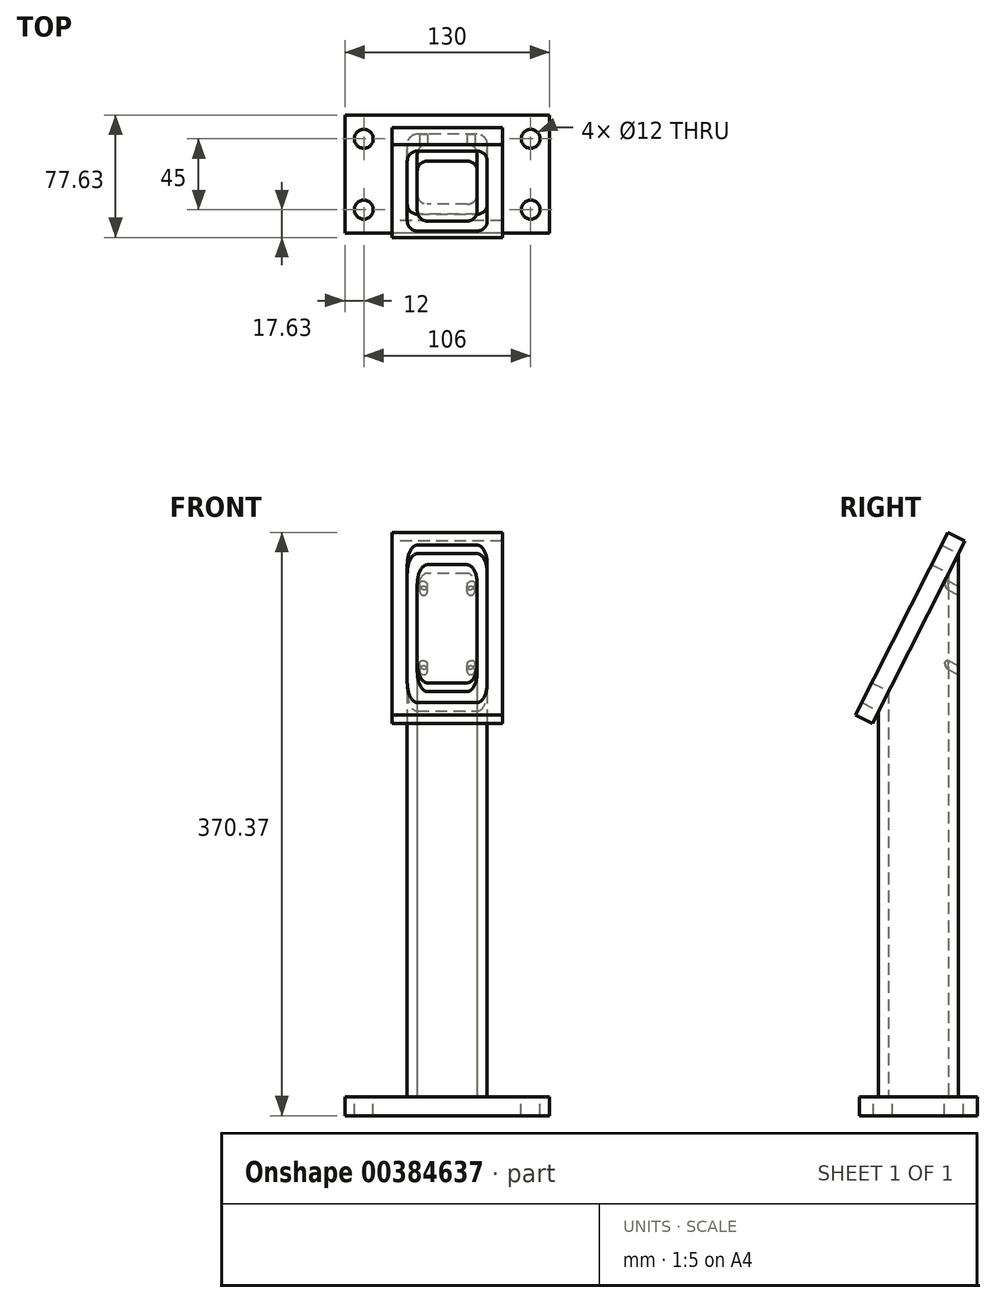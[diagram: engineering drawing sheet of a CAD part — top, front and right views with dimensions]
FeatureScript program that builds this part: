
annotation { "Feature Type Name" : "Feature", "Feature Type Description" : "" }
export const myFeature = defineFeature(function(context is Context, id is Id, definition is map)
    precondition{}
    {
        {
            var Q0;
            Q0=qCreatedBy(makeId("Top.planeOp"),FACE);
            var sketch = newSketch(context, id + "F0", { "sketchPlane" : qUnion([Q0])});
            skLineSegment(sketch, "E0.bottom", {"start": v(65, 37.5) * mm, "end": v(-65, 37.5) * mm});
            skLineSegment(sketch, "E0.top", {"start": v(65, -37.5) * mm, "end": v(-65, -37.5) * mm});
            skLineSegment(sketch, "E0.left", {"start": v(65, 37.5) * mm, "end": v(65, -37.5) * mm});
            skLineSegment(sketch, "E0.right", {"start": v(-65, 37.5) * mm, "end": v(-65, -37.5) * mm});
            skPoint(sketch, "E0.middle", {"position": v(0, 0) * mm});
            skSolve(sketch);
        }
        {
            var Q0;
            Q0=makeQuery(id+"F0.imprint","IMPRINT",FACE,{"disambiguationData":[TD([[makeQuery(id+"F0.imprint","IMPRINT",EDGE,{"derivedFrom":sQuery(id+"F0.wireOp",EDGE,"E0.bottom")}),1.0]])]});
            extrude(context, id + "F1", {"entities" : qUnion([Q0]), "depth" : -12 * mm});
        }
        {
            var Q0;
            Q0=makeQuery(id+"F1.opExtrude","CAP_FACE",FACE,{"disambiguationData":[OSD([sQuery(id+"F0.wireOp",EDGE,"E0.bottom"),sQuery(id+"F0.wireOp",EDGE,"E0.top"),sQuery(id+"F0.wireOp",EDGE,"E0.left"),sQuery(id+"F0.wireOp",EDGE,"E0.right")])],"isStart":true});
            var sketch = newSketch(context, id + "F2", { "sketchPlane" : qUnion([Q0])});
            skLineSegment(sketch, "E1.bottom", {"start": v(19.05, -25.4) * mm, "end": v(-19.05, -25.4) * mm});
            skLineSegment(sketch, "E1.top", {"start": v(19.05, 25.4) * mm, "end": v(-19.05, 25.4) * mm});
            skLineSegment(sketch, "E1.left", {"start": v(25.4, -19.05) * mm, "end": v(25.4, 19.05) * mm});
            skLineSegment(sketch, "E1.right", {"start": v(-25.4, -19.05) * mm, "end": v(-25.4, 19.05) * mm});
            skPoint(sketch, "E1.middle", {"position": v(0, 0) * mm});
            skPoint(sketch, "E2.visualSharp", {"position": v(-25.4, -25.4) * mm});
            skArc(sketch, "E2.filletArc", {"start": v(-25.4, -19.05) * mm, "mid": v(-23.54, -23.54) * mm, "end": v(-19.05, -25.4) * mm});
            skPoint(sketch, "E3.visualSharp", {"position": v(-25.4, 25.4) * mm});
            skArc(sketch, "E3.filletArc", {"start": v(-19.05, 25.4) * mm, "mid": v(-23.54, 23.54) * mm, "end": v(-25.4, 19.05) * mm});
            skPoint(sketch, "E4.visualSharp", {"position": v(25.4, 25.4) * mm});
            skArc(sketch, "E4.filletArc", {"start": v(25.4, 19.05) * mm, "mid": v(23.54, 23.54) * mm, "end": v(19.05, 25.4) * mm});
            skPoint(sketch, "E5.visualSharp", {"position": v(25.4, -25.4) * mm});
            skArc(sketch, "E5.filletArc", {"start": v(19.05, -25.4) * mm, "mid": v(23.54, -23.54) * mm, "end": v(25.4, -19.05) * mm});
            skLineSegment(sketch, "E6.bottom", {"start": v(12.7, 19.05) * mm, "end": v(-12.7, 19.05) * mm});
            skLineSegment(sketch, "E6.top", {"start": v(12.7, -19.05) * mm, "end": v(-12.7, -19.05) * mm});
            skLineSegment(sketch, "E6.left", {"start": v(19.05, 12.7) * mm, "end": v(19.05, -12.7) * mm});
            skLineSegment(sketch, "E6.right", {"start": v(-19.05, 12.7) * mm, "end": v(-19.05, -12.7) * mm});
            skArc(sketch, "E7.filletArc", {"start": v(-12.7, 19.05) * mm, "mid": v(-17.2, 17.2) * mm, "end": v(-19.05, 12.7) * mm});
            skArc(sketch, "E8.filletArc", {"start": v(19.05, 12.7) * mm, "mid": v(17.2, 17.2) * mm, "end": v(12.7, 19.05) * mm});
            skArc(sketch, "E9.filletArc", {"start": v(12.7, -19.05) * mm, "mid": v(17.2, -17.2) * mm, "end": v(19.05, -12.7) * mm});
            skArc(sketch, "E10.filletArc", {"start": v(-19.05, -12.7) * mm, "mid": v(-17.2, -17.2) * mm, "end": v(-12.7, -19.05) * mm});
            skSolve(sketch);
        }
        {
            var Q0;
            Q0=qSketchRegion(id+"F2",true);
            extrude(context, id + "F3", {"entities" : qUnion([Q0]), "operationType" : NewBodyOperationType.ADD, "depth" : 345 * mm});
        }
        {
            var Q0;
            {var subQ0=sQuery(id+"F0.wireOp",EDGE,"E0.left");var subQ1=sQuery(id+"F0.wireOp",EDGE,"E0.bottom");var subQ2=sQuery(id+"F0.wireOp",EDGE,"E0.right");var subQ3=sQuery(id+"F0.wireOp",EDGE,"E0.top");Q0=makeQuery(id+"F3.boolean.opBoolean","SPLIT",FACE,{"disambiguationData":[TD([makeQuery(id+"F1.opExtrude","SWEPT_FACE",FACE,{"disambiguationData":[OSD([subQ1])]})])],"derivedFrom":makeQuery(id+"F1.opExtrude","CAP_FACE",FACE,{"disambiguationData":[OSD([subQ1,subQ3,subQ0,subQ2])],"isStart":true})});}
            var sketch = newSketch(context, id + "F4", { "sketchPlane" : qUnion([Q0])});
            skLineSegment(sketch, "E11", {"start": v(-65, -37.5) * mm, "end": v(-53, -37.5) * mm, "construction": true});
            skLineSegment(sketch, "E12", {"start": v(-53, -37.5) * mm, "end": v(-53, -22.5) * mm, "construction": true});
            skLineSegment(sketch, "E13", {"start": v(-65, 37.5) * mm, "end": v(-53, 37.5) * mm, "construction": true});
            skLineSegment(sketch, "E14", {"start": v(-53, 37.5) * mm, "end": v(-53, 22.5) * mm, "construction": true});
            skLineSegment(sketch, "E15", {"start": v(65, 37.5) * mm, "end": v(53, 37.5) * mm, "construction": true});
            skLineSegment(sketch, "E16", {"start": v(65, -37.5) * mm, "end": v(53, -37.5) * mm, "construction": true});
            skLineSegment(sketch, "E17", {"start": v(53, -37.5) * mm, "end": v(53, -22.5) * mm, "construction": true});
            skLineSegment(sketch, "E18", {"start": v(53, 37.5) * mm, "end": v(53, 22.5) * mm, "construction": true});
            skSolve(sketch);
        }
        {
            var Q0;
            Q0=sQuery(id+"F4.wireOp",VERTEX,"E14.end");
            var Q1;
            Q1=sQuery(id+"F4.wireOp",VERTEX,"E18.end");
            var Q2;
            Q2=sQuery(id+"F4.wireOp",VERTEX,"E17.end");
            var Q3;
            Q3=sQuery(id+"F4.wireOp",VERTEX,"E12.end");
            var Q4;
            Q4=makeQuery(id+"F1.opExtrude","SWEPT_BODY",BODY,{"disambiguationData":[OSD([sQuery(id+"F0.wireOp",EDGE,"E0.bottom"),sQuery(id+"F0.wireOp",EDGE,"E0.top"),sQuery(id+"F0.wireOp",EDGE,"E0.left"),sQuery(id+"F0.wireOp",EDGE,"E0.right")])]});
            hole(context, id + "F5", {"style" : HoleStyle.SIMPLE, "endStyle" : HoleEndStyle.THROUGH, "holeDiameter" : 12 * mm, "isTappedThrough" : true, "tappedDepth" : 12 * mm, "tapClearance" : 3, "locations" : qUnion([Q0, Q1, Q2, Q3]), "scope" : qUnion([Q4])});
        }
        {
            var Q0;
            Q0=makeQuery(id+"F3.opExtrude","SWEPT_FACE",FACE,{"disambiguationData":[OSD([sQuery(id+"F2.wireOp",EDGE,"E1.left")])]});
            var sketch = newSketch(context, id + "F6", { "sketchPlane" : qUnion([Q0])});
            skLineSegment(sketch, "E19", {"start": v(-19.05, 345) * mm, "end": v(-25.4, 345) * mm, "construction": true});
            skLineSegment(sketch, "E20", {"start": v(-25.4, 345) * mm, "end": v(25.4, 345) * mm});
            skLineSegment(sketch, "E21", {"start": v(25.4, 345) * mm, "end": v(-25.4, 244.95) * mm});
            skLineSegment(sketch, "E22", {"start": v(-25.4, 345) * mm, "end": v(-25.4, 244.95) * mm});
            skSolve(sketch);
        }
        {
            var Q0;
            {var subQ3=sQuery(id+"F6.wireOp",EDGE,"E22");Q0=makeQuery(id+"F6.imprint","IMPRINT",FACE,{"disambiguationData":[TD([[makeQuery(id+"F6.imprint","IMPRINT",EDGE,{"derivedFrom":subQ3}),1.0]])]});}
            var Q1;
            {var subQ0=sQuery(id+"F6.wireOp",EDGE,"E20");var subQ1=sQuery(id+"F2.wireOp",EDGE,"E1.left");var subQ2=makeQuery(id+"F3.opExtrude","SWEPT_EDGE",EDGE,{"disambiguationData":[OSD([subQ1,sQuery(id+"F2.wireOp",EDGE,"E5.filletArc")])]});var subQ3=makeQuery(id+"F6.imprint","INTERSECT",VERTEX,{"derivedFrom":[subQ2,subQ0]});Q1=makeQuery(id+"F6.imprint","IMPRINT",FACE,{"disambiguationData":[TD([[makeQuery(id+"F6.imprint","IMPRINT",EDGE,{"disambiguationData":[TD([[subQ3,-1.0]])],"derivedFrom":subQ0}),-1.0]])]});}
            var Q2;
            {var subQ0=sQuery(id+"F6.wireOp",EDGE,"E20");var subQ3=sQuery(id+"F6.wireOp",EDGE,"E21");var subQ4=makeQuery(id+"F6.imprint","INTERSECT",VERTEX,{"derivedFrom":[subQ0,subQ3]});Q2=makeQuery(id+"F6.imprint","IMPRINT",FACE,{"disambiguationData":[TD([[makeQuery(id+"F6.imprint","IMPRINT",EDGE,{"disambiguationData":[TD([[subQ4,1.0]])],"derivedFrom":subQ0}),-1.0]])]});}
            extrude(context, id + "F7", {"entities" : qUnion([Q0, Q1, Q2]), "operationType" : NewBodyOperationType.REMOVE, "oppositeDirection" : true, "depth" : 50.8 * mm});
        }
        {
            var Q0;
            Q0=makeQuery(id+"F7.boolean.opBoolean","COPY",FACE,{"derivedFrom":makeQuery(id+"F7.opExtrude","SWEPT_FACE",FACE,{"disambiguationData":[OSD([sQuery(id+"F6.wireOp",EDGE,"E21")])]})});
            var sketch = newSketch(context, id + "F8", { "sketchPlane" : qUnion([Q0])});
            skLineSegment(sketch, "E23.bottom", {"start": v(35, 198.01) * mm, "end": v(-35, 198.01) * mm});
            skLineSegment(sketch, "E23.top", {"start": v(35, 328.01) * mm, "end": v(-35, 328.01) * mm});
            skLineSegment(sketch, "E23.left", {"start": v(35, 198.01) * mm, "end": v(35, 328.01) * mm});
            skLineSegment(sketch, "E23.right", {"start": v(-35, 198.01) * mm, "end": v(-35, 328.01) * mm});
            skPoint(sketch, "E23.middle", {"position": v(0, 263.01) * mm});
            skPoint(sketch, "E23.middle.positionSnap0", {"position": v(0, 305.09) * mm});
            skPoint(sketch, "E23.middle.positionSnap1", {"position": v(-19.05, 263.01) * mm});
            skPoint(sketch, "E23.centerSnap0", {"position": v(0, 305.09) * mm});
            skPoint(sketch, "E23.centerSnap1", {"position": v(-19.05, 263.01) * mm});
            skSolve(sketch);
        }
        {
            var Q0;
            {var subQ0=makeQuery(id+"F7.opExtrude","SWEPT_FACE",FACE,{"disambiguationData":[OSD([sQuery(id+"F6.wireOp",EDGE,"E21")])]});Q0=makeQuery(id+"F8.imprint","IMPRINT",FACE,{"disambiguationData":[TD([[makeQuery(id+"F8.imprint","IMPRINT",EDGE,{"derivedFrom":makeQuery(id+"F7.boolean.opBoolean","INTERSECT",EDGE,{"derivedFrom":[makeQuery(id+"F3.opExtrude","SWEPT_FACE",FACE,{"disambiguationData":[OSD([sQuery(id+"F2.wireOp",EDGE,"E6.bottom")])]}),subQ0]})}),1.0]])]});}
            var Q1;
            {var subQ0=sQuery(id+"F6.wireOp",EDGE,"E21");Q1=makeQuery(id+"F8.imprint","IMPRINT",FACE,{"disambiguationData":[TD([[makeQuery(id+"F8.imprint","IMPRINT",EDGE,{"derivedFrom":makeQuery(id+"F7.boolean.opBoolean","COPY",EDGE,{"derivedFrom":makeQuery(id+"F7.opExtrude","CAP_EDGE",EDGE,{"disambiguationData":[OSD([subQ0])],"isStart":true})})}),-1.0]])]});}
            var Q2;
            Q2=makeQuery(id+"F8.imprint","IMPRINT",FACE,{"disambiguationData":[TD([[makeQuery(id+"F8.imprint","IMPRINT",EDGE,{"derivedFrom":sQuery(id+"F8.wireOp",EDGE,"E23.bottom")}),-1.0]])]});
            extrude(context, id + "F9", {"entities" : qUnion([Q0, Q1, Q2]), "operationType" : NewBodyOperationType.ADD, "depth" : 12 * mm});
        }
        {
            var Q0;
            Q0=makeQuery(id+"F9.opExtrude","CAP_FACE",FACE,{"disambiguationData":[OSD([sQuery(id+"F8.wireOp",EDGE,"E23.bottom"),sQuery(id+"F8.wireOp",EDGE,"E23.top"),sQuery(id+"F8.wireOp",EDGE,"E23.left"),sQuery(id+"F8.wireOp",EDGE,"E23.right")])],"isStart":false});
            var sketch = newSketch(context, id + "F10", { "sketchPlane" : qUnion([Q0])});
            skLineSegment(sketch, "E24", {"start": v(35, 328.01) * mm, "end": v(35, 298.01) * mm, "construction": true});
            skLineSegment(sketch, "E25", {"start": v(35, 298.01) * mm, "end": v(15, 298.01) * mm, "construction": true});
            skLineSegment(sketch, "E26", {"start": v(15, 298.01) * mm, "end": v(-15, 298.01) * mm, "construction": true});
            skLineSegment(sketch, "E27", {"start": v(15, 298.01) * mm, "end": v(15, 253.01) * mm, "construction": true});
            skLineSegment(sketch, "E28", {"start": v(15, 253.01) * mm, "end": v(-15, 253.01) * mm, "construction": true});
            skSolve(sketch);
        }
        {
            var Q0;
            Q0=sQuery(id+"F10.wireOp",VERTEX,"E27.start");
            var Q1;
            Q1=sQuery(id+"F10.wireOp",VERTEX,"E28.start");
            var Q2;
            Q2=sQuery(id+"F10.wireOp",VERTEX,"E28.end");
            var Q3;
            Q3=sQuery(id+"F10.wireOp",VERTEX,"E26.end");
            var Q4;
            Q4=makeQuery(id+"F1.opExtrude","SWEPT_BODY",BODY,{"disambiguationData":[OSD([sQuery(id+"F0.wireOp",EDGE,"E0.bottom"),sQuery(id+"F0.wireOp",EDGE,"E0.top"),sQuery(id+"F0.wireOp",EDGE,"E0.left"),sQuery(id+"F0.wireOp",EDGE,"E0.right")])]});
            hole(context, id + "F11", {"style" : HoleStyle.SIMPLE, "endStyle" : HoleEndStyle.BLIND, "holeDiameter" : 5 * mm, "holeDepth" : 8 * mm, "isTappedThrough" : true, "tappedDepth" : 12 * mm, "tapClearance" : 3, "locations" : qUnion([Q0, Q1, Q2, Q3]), "scope" : qUnion([Q4])});
        }
    });
